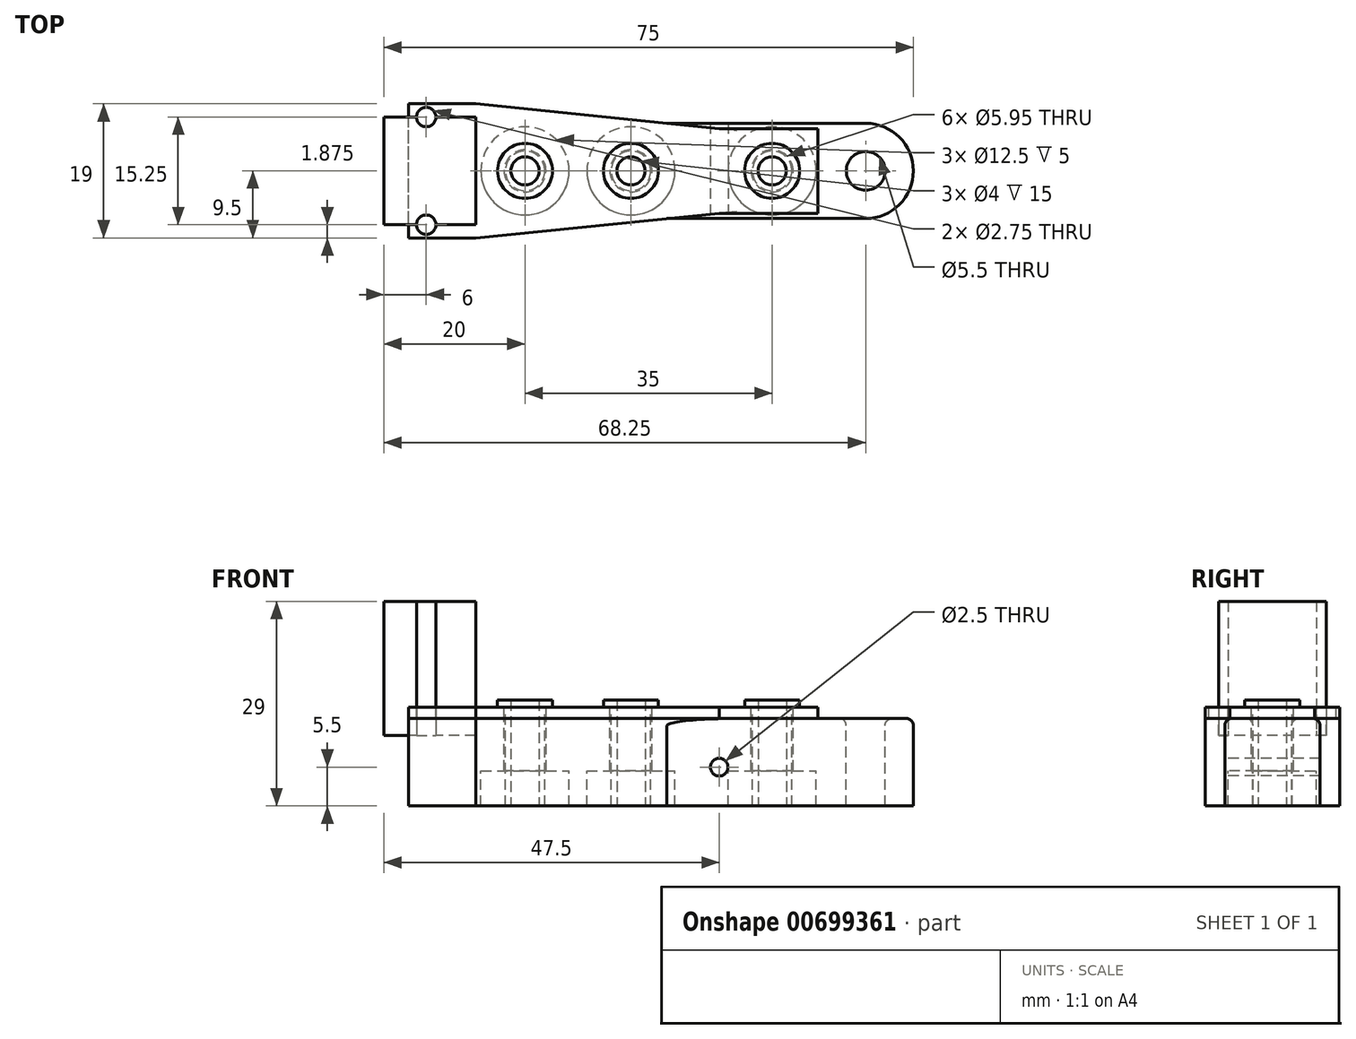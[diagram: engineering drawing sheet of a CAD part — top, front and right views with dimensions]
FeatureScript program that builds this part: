
annotation { "Feature Type Name" : "Feature", "Feature Type Description" : "" }
export const myFeature = defineFeature(function(context is Context, id is Id, definition is map)
    precondition{}
    {
        {
            var Q0;
            Q0=qCreatedBy(makeId("Top.planeOp"),FACE);
            var sketch = newSketch(context, id + "F0", { "sketchPlane" : qUnion([Q0])});
            skCircle(sketch, "E0", {"center": v(-17.5, 0) * mm, "radius": 2 * mm});
            skCircle(sketch, "E1", {"center": v(-17.5, 0) * mm, "radius": 2.8 * mm});
            skCircle(sketch, "E2", {"center": v(-17.5, 0) * mm, "radius": 3.9 * mm});
            skCircle(sketch, "E3", {"center": v(-2.5, 0) * mm, "radius": 2 * mm});
            skCircle(sketch, "E4", {"center": v(-2.5, 0) * mm, "radius": 2.8 * mm});
            skCircle(sketch, "E5", {"center": v(-2.5, 0) * mm, "radius": 3.9 * mm});
            skCircle(sketch, "E6", {"center": v(17.5, 0) * mm, "radius": 2 * mm});
            skCircle(sketch, "E7", {"center": v(17.5, 0) * mm, "radius": 2.8 * mm});
            skCircle(sketch, "E8", {"center": v(17.5, 0) * mm, "radius": 3.9 * mm});
            skLineSegment(sketch, "E9", {"start": v(0, 7.52) * mm, "end": v(0, -7.52) * mm, "construction": true});
            skLineSegment(sketch, "E10", {"start": v(10, 5.5) * mm, "end": v(10, -3.3) * mm, "construction": true});
            skSolve(sketch);
        }
        {
            var Q0;
            Q0 = qSketchRegion(id + "F0", true);
            var Q1;
            Q1=makeQuery(id+"F0.imprint","IMPRINT",FACE,{"disambiguationData":[TD([[makeQuery(id+"F0.imprint","IMPRINT",EDGE,{"derivedFrom":sQuery(id+"F0.wireOp",EDGE,"E0")}),-1.0]])]});
            var Q2;
            Q2=makeQuery(id+"F0.imprint","IMPRINT",FACE,{"disambiguationData":[TD([[makeQuery(id+"F0.imprint","IMPRINT",EDGE,{"derivedFrom":sQuery(id+"F0.wireOp",EDGE,"E3")}),-1.0]])]});
            var Q3;
            Q3=makeQuery(id+"F0.imprint","IMPRINT",FACE,{"disambiguationData":[TD([[makeQuery(id+"F0.imprint","IMPRINT",EDGE,{"derivedFrom":sQuery(id+"F0.wireOp",EDGE,"E6")}),-1.0]])]});
            extrude(context, id + "F1", {"entities" : qUnion([Q0, Q1, Q2, Q3]), "depth" : 1 * mm, "offsetDistance" : 25 * mm});
        }
        {
            var Q0;
            Q0=makeQuery(id+"F0.imprint","IMPRINT",FACE,{"disambiguationData":[TD([[makeQuery(id+"F0.imprint","IMPRINT",EDGE,{"derivedFrom":sQuery(id+"F0.wireOp",EDGE,"E0")}),-1.0]])]});
            var Q1;
            Q1=makeQuery(id+"F0.imprint","IMPRINT",FACE,{"disambiguationData":[TD([[makeQuery(id+"F0.imprint","IMPRINT",EDGE,{"derivedFrom":sQuery(id+"F0.wireOp",EDGE,"E3")}),-1.0]])]});
            var Q2;
            Q2=makeQuery(id+"F0.imprint","IMPRINT",FACE,{"disambiguationData":[TD([[makeQuery(id+"F0.imprint","IMPRINT",EDGE,{"derivedFrom":sQuery(id+"F0.wireOp",EDGE,"E6")}),-1.0]])]});
            extrude(context, id + "F2", {"entities" : qUnion([Q0, Q1, Q2]), "operationType" : NewBodyOperationType.ADD, "oppositeDirection" : true, "depth" : 14 * mm, "offsetDistance" : 25 * mm});
        }
        {
            var Q0;
            Q0=qCreatedBy(makeId("Top.planeOp"),FACE);
            var sketch = newSketch(context, id + "F3", { "sketchPlane" : qUnion([Q0])});
            skLineSegment(sketch, "E11.bottom", {"start": v(-24.5, 7.62) * mm, "end": v(-37.5, 7.62) * mm});
            skLineSegment(sketch, "E11.top", {"start": v(-24.5, -7.63) * mm, "end": v(-37.5, -7.63) * mm});
            skLineSegment(sketch, "E11.left", {"start": v(-24.5, 7.62) * mm, "end": v(-24.5, -7.63) * mm});
            skLineSegment(sketch, "E11.right", {"start": v(-37.5, 7.62) * mm, "end": v(-37.5, -7.63) * mm});
            skPoint(sketch, "E11.middle", {"position": v(-31, 0) * mm});
            skCircle(sketch, "E12", {"center": v(-31.5, 7.62) * mm, "radius": 1.38 * mm});
            skCircle(sketch, "E13", {"center": v(-31.5, -7.62) * mm, "radius": 1.38 * mm});
            skLineSegment(sketch, "E14.bottom", {"start": v(-25.5, -4.5) * mm, "end": v(-29.5, -4.5) * mm});
            skLineSegment(sketch, "E14.top", {"start": v(-25.5, 4.5) * mm, "end": v(-29.5, 4.5) * mm});
            skLineSegment(sketch, "E14.left", {"start": v(-25.5, -4.5) * mm, "end": v(-25.5, 4.5) * mm});
            skLineSegment(sketch, "E14.right", {"start": v(-29.5, -4.5) * mm, "end": v(-29.5, 4.5) * mm});
            skPoint(sketch, "E14.middle", {"position": v(-27.5, 0) * mm});
            skSolve(sketch);
        }
        {
            var Q0;
            {var subQ0=sQuery(id+"F3.wireOp",EDGE,"E11.left");Q0=makeQuery(id+"F3.imprint","IMPRINT",FACE,{"disambiguationData":[TD([[makeQuery(id+"F3.imprint","IMPRINT",EDGE,{"derivedFrom":subQ0}),-1.0]])]});}
            var Q1;
            {var subQ0=sQuery(id+"F3.wireOp",EDGE,"E12");var subQ1=sQuery(id+"F3.wireOp",EDGE,"E11.bottom");var subQ2=makeQuery(id+"F3.imprint","INTERSECT",VERTEX,{"disambiguationData":[OD(0.0)],"derivedFrom":[subQ1,subQ0]});Q1=makeQuery(id+"F3.imprint","IMPRINT",FACE,{"disambiguationData":[TD([[makeQuery(id+"F3.imprint","IMPRINT",EDGE,{"disambiguationData":[TD([[subQ2,-1.0]])],"derivedFrom":subQ1}),1.0]])]});}
            var Q2;
            {var subQ0=sQuery(id+"F3.wireOp",EDGE,"E13");var subQ1=sQuery(id+"F3.wireOp",EDGE,"E11.top");var subQ2=makeQuery(id+"F3.imprint","INTERSECT",VERTEX,{"disambiguationData":[OD(0.0)],"derivedFrom":[subQ1,subQ0]});Q2=makeQuery(id+"F3.imprint","IMPRINT",FACE,{"disambiguationData":[TD([[makeQuery(id+"F3.imprint","IMPRINT",EDGE,{"disambiguationData":[TD([[subQ2,-1.0]])],"derivedFrom":subQ1}),-1.0]])]});}
            var Q3;
            Q3=makeQuery(id+"F3.imprint","IMPRINT",FACE,{"disambiguationData":[TD([[makeQuery(id+"F3.imprint","IMPRINT",EDGE,{"derivedFrom":sQuery(id+"F3.wireOp",EDGE,"E14.bottom")}),-1.0]])]});
            extrude(context, id + "F4", {"entities" : qUnion([Q0, Q1, Q2, Q3]), "depth" : 15 * mm, "offsetDistance" : 25 * mm});
        }
        {
            var Q0;
            {var subQ0=sQuery(id+"F3.wireOp",EDGE,"E13");var subQ1=sQuery(id+"F3.wireOp",EDGE,"E11.top");var subQ2=makeQuery(id+"F3.imprint","INTERSECT",VERTEX,{"disambiguationData":[OD(0.0)],"derivedFrom":[subQ1,subQ0]});Q0=makeQuery(id+"F3.imprint","IMPRINT",FACE,{"disambiguationData":[TD([[makeQuery(id+"F3.imprint","IMPRINT",EDGE,{"disambiguationData":[TD([[subQ2,-1.0]])],"derivedFrom":subQ1}),1.0]])]});}
            var Q1;
            {var subQ0=sQuery(id+"F3.wireOp",EDGE,"E13");var subQ1=sQuery(id+"F3.wireOp",EDGE,"E11.top");var subQ2=makeQuery(id+"F3.imprint","INTERSECT",VERTEX,{"disambiguationData":[OD(0.0)],"derivedFrom":[subQ1,subQ0]});Q1=makeQuery(id+"F3.imprint","IMPRINT",FACE,{"disambiguationData":[TD([[makeQuery(id+"F3.imprint","IMPRINT",EDGE,{"disambiguationData":[TD([[subQ2,-1.0]])],"derivedFrom":subQ1}),-1.0]])]});}
            var Q2;
            {var subQ0=sQuery(id+"F3.wireOp",EDGE,"E12");var subQ1=sQuery(id+"F3.wireOp",EDGE,"E11.bottom");var subQ2=makeQuery(id+"F3.imprint","INTERSECT",VERTEX,{"disambiguationData":[OD(0.0)],"derivedFrom":[subQ1,subQ0]});Q2=makeQuery(id+"F3.imprint","IMPRINT",FACE,{"disambiguationData":[TD([[makeQuery(id+"F3.imprint","IMPRINT",EDGE,{"disambiguationData":[TD([[subQ2,-1.0]])],"derivedFrom":subQ1}),1.0]])]});}
            var Q3;
            {var subQ0=sQuery(id+"F3.wireOp",EDGE,"E12");var subQ1=sQuery(id+"F3.wireOp",EDGE,"E11.bottom");var subQ2=makeQuery(id+"F3.imprint","INTERSECT",VERTEX,{"disambiguationData":[OD(0.0)],"derivedFrom":[subQ1,subQ0]});Q3=makeQuery(id+"F3.imprint","IMPRINT",FACE,{"disambiguationData":[TD([[makeQuery(id+"F3.imprint","IMPRINT",EDGE,{"disambiguationData":[TD([[subQ2,-1.0]])],"derivedFrom":subQ1}),-1.0]])]});}
            var Q4;
            Q4=makeQuery(id+"F3.imprint","IMPRINT",FACE,{"disambiguationData":[TD([[makeQuery(id+"F3.imprint","IMPRINT",EDGE,{"derivedFrom":sQuery(id+"F3.wireOp",EDGE,"E14.bottom")}),-1.0]])]});
            extrude(context, id + "F5", {"entities" : qUnion([Q0, Q1, Q2, Q3, Q4]), "operationType" : NewBodyOperationType.ADD, "oppositeDirection" : true, "depth" : 4 * mm, "offsetDistance" : 25 * mm});
        }
        {
            var Q0;
            Q0=qCreatedBy(makeId("Top.planeOp"),FACE);
            var sketch = newSketch(context, id + "F6", { "sketchPlane" : qUnion([Q0])});
            skLineSegment(sketch, "E15", {"start": v(-34, 9.5) * mm, "end": v(-34, -9.5) * mm});
            skLineSegment(sketch, "E16", {"start": v(-34, -9.5) * mm, "end": v(-24.5, -9.5) * mm});
            skLineSegment(sketch, "E17", {"start": v(-24.5, -9.5) * mm, "end": v(10, -6) * mm});
            skLineSegment(sketch, "E18", {"start": v(10, -6) * mm, "end": v(24, -6) * mm});
            skLineSegment(sketch, "E19", {"start": v(24, -6) * mm, "end": v(24, 6) * mm});
            skLineSegment(sketch, "E20", {"start": v(-34, 0) * mm, "end": v(24, 0) * mm, "construction": true});
            skLineSegment(sketch, "E21.MirrorCS", {"start": v(10, 6) * mm, "end": v(24, 6) * mm});
            skLineSegment(sketch, "E22.MirrorCS", {"start": v(-24.5, 9.5) * mm, "end": v(10, 6) * mm});
            skLineSegment(sketch, "E23.MirrorCS", {"start": v(-34, 9.5) * mm, "end": v(-24.5, 9.5) * mm});
            skCircle(sketch, "E24", {"center": v(-17.5, 0) * mm, "radius": 2.98 * mm});
            skCircle(sketch, "E25", {"center": v(-2.5, 0) * mm, "radius": 2.98 * mm});
            skCircle(sketch, "E26", {"center": v(17.5, 0) * mm, "radius": 2.98 * mm});
            skCircle(sketch, "E27.0", {"center": v(-31.5, -7.62) * mm, "radius": 1.38 * mm});
            skCircle(sketch, "E27.1", {"center": v(-31.5, 7.62) * mm, "radius": 1.38 * mm});
            skSolve(sketch);
        }
        {
            var Q0;
            Q0 = qSketchRegion(id + "F6", true);
            extrude(context, id + "F7", {"entities" : qUnion([Q0]), "oppositeDirection" : true, "depth" : 1.6 * mm, "offsetDistance" : 25 * mm});
        }
        {
            var Q0;
            Q0=makeQuery(id+"F7.opExtrude","CAP_FACE",FACE,{"disambiguationData":[OSD([sQuery(id+"F6.wireOp",EDGE,"E15"),sQuery(id+"F6.wireOp",EDGE,"E16"),sQuery(id+"F6.wireOp",EDGE,"E17"),sQuery(id+"F6.wireOp",EDGE,"E18"),sQuery(id+"F6.wireOp",EDGE,"E19"),sQuery(id+"F6.wireOp",EDGE,"E23.MirrorCS"),sQuery(id+"F6.wireOp",EDGE,"E22.MirrorCS"),sQuery(id+"F6.wireOp",EDGE,"E21.MirrorCS"),sQuery(id+"F6.wireOp",EDGE,"E24"),sQuery(id+"F6.wireOp",EDGE,"E25"),sQuery(id+"F6.wireOp",EDGE,"E26"),sQuery(id+"F6.wireOp",EDGE,"E27.0"),sQuery(id+"F6.wireOp",EDGE,"E27.1")])],"isStart":false});
            var sketch = newSketch(context, id + "F8", { "sketchPlane" : qUnion([Q0])});
            skLineSegment(sketch, "E28.bottom", {"start": v(30.75, 6.75) * mm, "end": v(2.6, 6.75) * mm});
            skLineSegment(sketch, "E28.top", {"start": v(30.75, -6.75) * mm, "end": v(2.6, -6.75) * mm});
            skPoint(sketch, "E28.middle", {"position": v(0, 0) * mm});
            skLineSegment(sketch, "E29.0", {"start": v(-34, 9.5) * mm, "end": v(-24.5, 9.5) * mm});
            skLineSegment(sketch, "E29.1", {"start": v(-34, -9.5) * mm, "end": v(-34, 9.5) * mm});
            skLineSegment(sketch, "E29.2", {"start": v(-34, -9.5) * mm, "end": v(-24.5, -9.5) * mm});
            skLineSegment(sketch, "E30", {"start": v(-24.5, 9.5) * mm, "end": v(2.6, 6.75) * mm});
            skLineSegment(sketch, "E31", {"start": v(-24.5, -9.5) * mm, "end": v(2.6, -6.75) * mm});
            skPoint(sketch, "E28.right.start.orphan", {"position": v(-30.75, 6.75) * mm});
            skPoint(sketch, "E32.orphan", {"position": v(-30.75, -6.75) * mm});
            skArc(sketch, "E33", {"start": v(30.75, -6.75) * mm, "mid": v(37.5, 0) * mm, "end": v(30.75, 6.75) * mm});
            skCircle(sketch, "E34", {"center": v(30.75, 0) * mm, "radius": 2.75 * mm});
            skCircle(sketch, "E35.0", {"center": v(-17.5, 0) * mm, "radius": 2.98 * mm});
            skCircle(sketch, "E35.1", {"center": v(-2.5, 0) * mm, "radius": 2.98 * mm});
            skCircle(sketch, "E35.2", {"center": v(17.5, 0) * mm, "radius": 2.98 * mm});
            skSolve(sketch);
        }
        {
            var Q0;
            Q0 = qSketchRegion(id + "F8", true);
            extrude(context, id + "F9", {"entities" : qUnion([Q0]), "depth" : 7.4 * mm, "offsetDistance" : 25 * mm});
        }
        {
            var Q0;
            Q0=makeQuery(id+"F9.opExtrude","CAP_FACE",FACE,{"disambiguationData":[OSD([sQuery(id+"F8.wireOp",EDGE,"E28.bottom"),sQuery(id+"F8.wireOp",EDGE,"E28.top"),sQuery(id+"F8.wireOp",EDGE,"E29.0"),sQuery(id+"F8.wireOp",EDGE,"E29.1"),sQuery(id+"F8.wireOp",EDGE,"E29.2"),sQuery(id+"F8.wireOp",EDGE,"E30"),sQuery(id+"F8.wireOp",EDGE,"E31"),sQuery(id+"F8.wireOp",EDGE,"E33"),sQuery(id+"F8.wireOp",EDGE,"E34"),sQuery(id+"F8.wireOp",EDGE,"E35.0"),sQuery(id+"F8.wireOp",EDGE,"E35.1"),sQuery(id+"F8.wireOp",EDGE,"E35.2")])],"isStart":false});
            var sketch = newSketch(context, id + "F10", { "sketchPlane" : qUnion([Q0])});
            skCircle(sketch, "E36", {"center": v(-17.5, 0) * mm, "radius": 6.25 * mm});
            skCircle(sketch, "E37", {"center": v(-2.5, 0) * mm, "radius": 6.25 * mm});
            skCircle(sketch, "E38", {"center": v(17.5, 0) * mm, "radius": 6.25 * mm});
            skLineSegment(sketch, "E39.0", {"start": v(-34, 9.5) * mm, "end": v(-24.5, 9.5) * mm});
            skLineSegment(sketch, "E39.1", {"start": v(-24.5, 9.5) * mm, "end": v(2.6, 6.75) * mm});
            skLineSegment(sketch, "E39.2", {"start": v(30.75, 6.75) * mm, "end": v(2.6, 6.75) * mm});
            skArc(sketch, "E39.3", {"start": v(30.75, -6.75) * mm, "mid": v(37.5, 0) * mm, "end": v(30.75, 6.75) * mm});
            skLineSegment(sketch, "E39.4", {"start": v(30.75, -6.75) * mm, "end": v(2.6, -6.75) * mm});
            skLineSegment(sketch, "E39.5", {"start": v(-24.5, -9.5) * mm, "end": v(2.6, -6.75) * mm});
            skLineSegment(sketch, "E39.6", {"start": v(-34, -9.5) * mm, "end": v(-24.5, -9.5) * mm});
            skLineSegment(sketch, "E39.7", {"start": v(-34, -9.5) * mm, "end": v(-34, 9.5) * mm});
            skCircle(sketch, "E40.0", {"center": v(30.75, 0) * mm, "radius": 2.75 * mm});
            skSolve(sketch);
        }
        {
            var Q0;
            Q0 = qSketchRegion(id + "F10", true);
            var Q1;
            Q1=makeQuery(id+"F2.opExtrude","CAP_FACE",FACE,{"disambiguationData":[OSD([sQuery(id+"F0.wireOp",EDGE,"E0"),sQuery(id+"F0.wireOp",EDGE,"E1")])],"isStart":false});
            extrude(context, id + "F11", {"entities" : qUnion([Q0]), "operationType" : NewBodyOperationType.ADD, "endBound" : BoundingType.UP_TO_SURFACE, "depth" : 25 * mm, "endBoundEntityFace" : qUnion([Q1]), "offsetDistance" : 25 * mm});
        }
        {
            var Q0;
            Q0=makeQuery(id+"F7.opExtrude","SWEPT_FACE",FACE,{"disambiguationData":[OSD([sQuery(id+"F6.wireOp",EDGE,"E16")])]});
            var sketch = newSketch(context, id + "F12", { "sketchPlane" : qUnion([Q0])});
            skCircle(sketch, "E41", {"center": v(10, -8.5) * mm, "radius": 1.25 * mm});
            skSolve(sketch);
        }
        {
            var Q0;
            Q0 = qSketchRegion(id + "F12", true);
            var Q1;
            Q1=makeQuery(id+"F9.opExtrude","SWEPT_FACE",FACE,{"disambiguationData":[OSD([sQuery(id+"F8.wireOp",EDGE,"E28.top")])]});
            extrude(context, id + "F13", {"entities" : qUnion([Q0]), "operationType" : NewBodyOperationType.REMOVE, "endBound" : BoundingType.UP_TO_SURFACE, "oppositeDirection" : true, "depth" : 25 * mm, "endBoundEntityFace" : qUnion([Q1]), "offsetDistance" : 25 * mm});
        }
        {
            var Q0;
            Q0=makeQuery(id+"F4.opExtrude","SWEPT_BODY",BODY,{"disambiguationData":[OSD([sQuery(id+"F3.wireOp",EDGE,"E11.bottom"),sQuery(id+"F3.wireOp",EDGE,"E11.top"),sQuery(id+"F3.wireOp",EDGE,"E11.left"),sQuery(id+"F3.wireOp",EDGE,"E11.right")])]});
            var Q1;
            Q1=makeQuery(id+"F9.opExtrude","SWEPT_BODY",BODY,{"disambiguationData":[OSD([sQuery(id+"F8.wireOp",EDGE,"E28.bottom"),sQuery(id+"F8.wireOp",EDGE,"E28.top"),sQuery(id+"F8.wireOp",EDGE,"E29.0"),sQuery(id+"F8.wireOp",EDGE,"E29.1"),sQuery(id+"F8.wireOp",EDGE,"E29.2"),sQuery(id+"F8.wireOp",EDGE,"E30"),sQuery(id+"F8.wireOp",EDGE,"E31"),sQuery(id+"F8.wireOp",EDGE,"E33"),sQuery(id+"F8.wireOp",EDGE,"E34")])]});
            booleanBodies(context, id + "F14", {"operationType" : BooleanOperationType.SUBTRACTION, "tools" : qUnion([Q0]), "targets" : qUnion([Q1]), "keepTools" : true});
        }
        {
            var Q0;
            Q0=makeQuery(id+"F11.opExtrude","CAP_FACE",FACE,{"disambiguationData":[OSD([sQuery(id+"F0.wireOp",EDGE,"E0"),sQuery(id+"F0.wireOp",EDGE,"E1")])],"isStart":false});
            var Q1;
            Q1=makeQuery(id+"F9.opExtrude","CAP_EDGE",EDGE,{"disambiguationData":[OSD([sQuery(id+"F8.wireOp",EDGE,"E34")])],"isStart":true});
            var Q2;
            Q2=makeQuery(id+"F9.opExtrude","CAP_EDGE",EDGE,{"disambiguationData":[OSD([sQuery(id+"F8.wireOp",EDGE,"E33")])],"isStart":true});
            fillet(context, id + "F15", {"entities" : qUnion([Q0, Q1, Q2]), "radius" : 1 * mm, "tangentPropagation" : true, "allowEdgeOverflow" : false});
        }
    });
